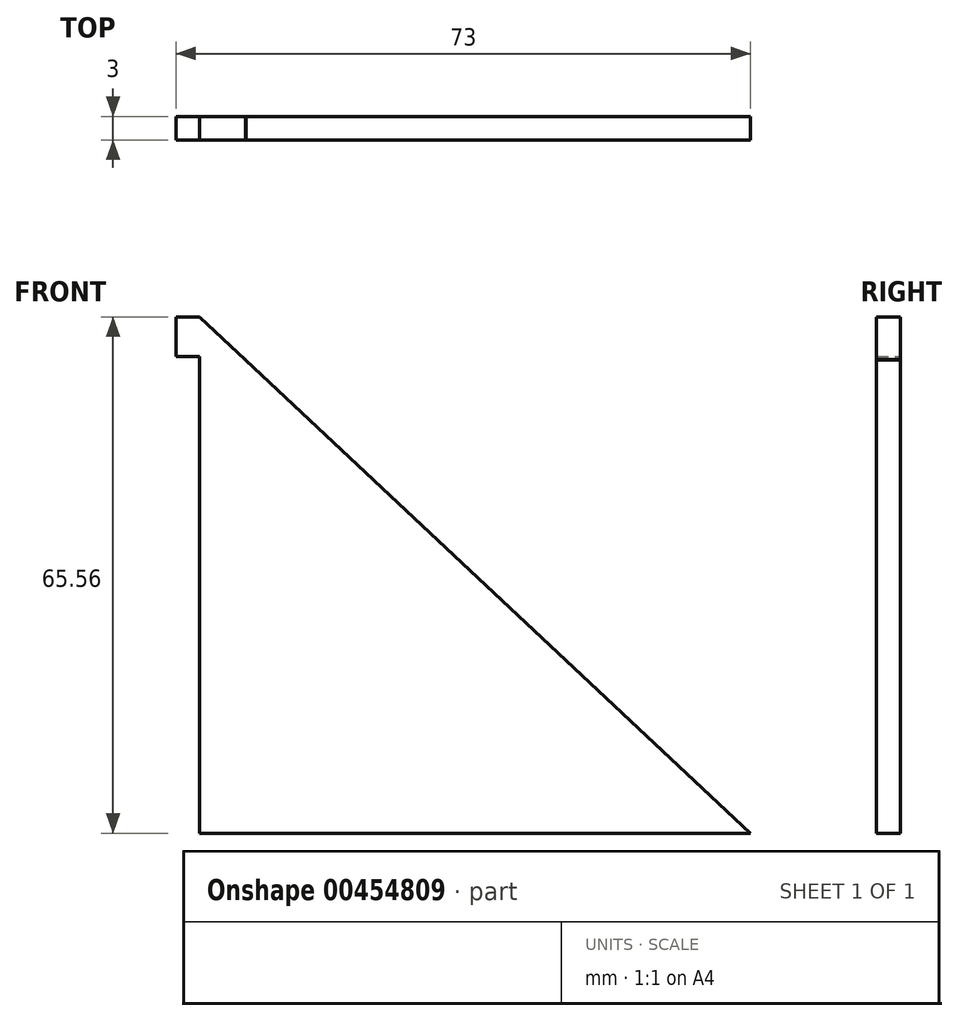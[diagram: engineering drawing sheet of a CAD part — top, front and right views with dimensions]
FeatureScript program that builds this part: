
annotation { "Feature Type Name" : "Feature", "Feature Type Description" : "" }
export const myFeature = defineFeature(function(context is Context, id is Id, definition is map)
    precondition{}
    {
        {
            var Q0;
            Q0=qCreatedBy(makeId("Front.planeOp"),FACE);
            var sketch = newSketch(context, id + "F0", { "sketchPlane" : qUnion([Q0])});
            skLineSegment(sketch, "E0", {"start": v(0, 18.6) * mm, "end": v(0, 14.59) * mm});
            skLineSegment(sketch, "E1", {"start": v(0, -46.96) * mm, "end": v(70, -46.96) * mm});
            skLineSegment(sketch, "E2", {"start": v(0, 18.6) * mm, "end": v(0.8, 17.84) * mm});
            skArc(sketch, "E3", {"start": v(0.8, 17.84) * mm, "mid": v(0.32, 17.16) * mm, "end": v(0, 16.38) * mm});
            skArc(sketch, "E4", {"start": v(5.88, 13.2) * mm, "mid": v(5.83, 13.14) * mm, "end": v(5.78, 13.08) * mm});
            skLineSegment(sketch, "E5.trimOffspring", {"start": v(66.42, -43.61) * mm, "end": v(70, -46.96) * mm});
            skLineSegment(sketch, "E6.trimOffspring", {"start": v(48.04, -26.4) * mm, "end": v(48.6, -26.93) * mm});
            skLineSegment(sketch, "E7.trimOffspring", {"start": v(32.07, -11.44) * mm, "end": v(32.32, -11.68) * mm});
            skLineSegment(sketch, "E8.trimOffspring", {"start": v(21.86, -1.88) * mm, "end": v(21.9, -1.92) * mm});
            skLineSegment(sketch, "E9.trimOffspring", {"start": v(13.51, 5.94) * mm, "end": v(13.78, 5.69) * mm});
            skLineSegment(sketch, "E10.trimOffspring", {"start": v(5.83, 13.14) * mm, "end": v(5.83, 13.14) * mm});
            skLineSegment(sketch, "E11", {"start": v(0, 18.6) * mm, "end": v(-3, 18.6) * mm});
            skLineSegment(sketch, "E12", {"start": v(-3, 18.6) * mm, "end": v(-3, 13.6) * mm});
            skLineSegment(sketch, "E13", {"start": v(-3, 13.6) * mm, "end": v(0, 13.6) * mm});
            skLineSegment(sketch, "E14", {"start": v(0.8, 17.84) * mm, "end": v(70, -46.96) * mm});
            skArc(sketch, "E15.trimOffspring", {"start": v(5.78, 13.08) * mm, "mid": v(5.83, 13.14) * mm, "end": v(5.88, 13.2) * mm});
            skLineSegment(sketch, "E16.trimOffspring", {"start": v(0, 13.6) * mm, "end": v(0, -46.96) * mm});
            skSolve(sketch);
        }
        {
            var Q0;
            Q0 = qSketchRegion(id + "F0", true);
            extrude(context, id + "F1", {"entities" : qUnion([Q0]), "depth" : 3 * mm});
        }
    });
